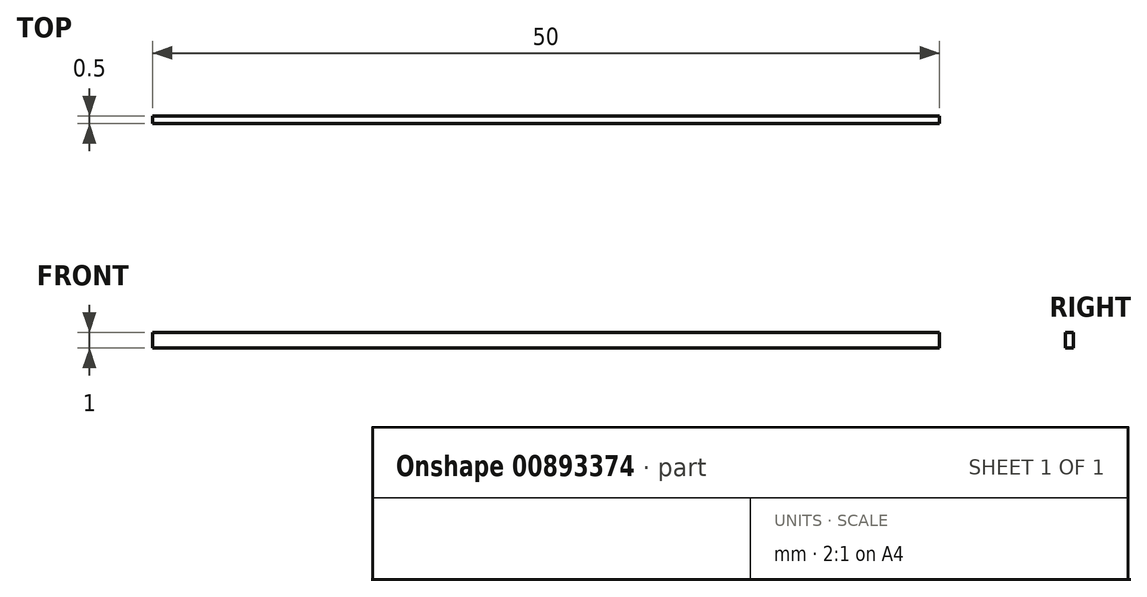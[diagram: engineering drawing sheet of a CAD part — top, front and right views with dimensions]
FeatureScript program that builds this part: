
annotation { "Feature Type Name" : "Feature", "Feature Type Description" : "" }
export const myFeature = defineFeature(function(context is Context, id is Id, definition is map)
    precondition{}
    {
        {
            var Q0;
            Q0=qCreatedBy(makeId("Front.planeOp"),FACE);
            var sketch = newSketch(context, id + "F0", { "sketchPlane" : qUnion([Q0])});
            skLineSegment(sketch, "E0.bottom", {"start": v(25, 0.5) * mm, "end": v(-25, 0.5) * mm});
            skLineSegment(sketch, "E0.top", {"start": v(25, -0.5) * mm, "end": v(-25, -0.5) * mm});
            skLineSegment(sketch, "E0.left", {"start": v(25, 0.5) * mm, "end": v(25, -0.5) * mm});
            skLineSegment(sketch, "E0.right", {"start": v(-25, 0.5) * mm, "end": v(-25, -0.5) * mm});
            skPoint(sketch, "E0.middle", {"position": v(0, 0) * mm});
            skSolve(sketch);
        }
        {
            var Q0;
            Q0 = qSketchRegion(id + "F0", true);
            extrude(context, id + "F1", {"entities" : qUnion([Q0]), "depth" : 0.5 * mm, "offsetDistance" : 25 * mm});
        }
    });
